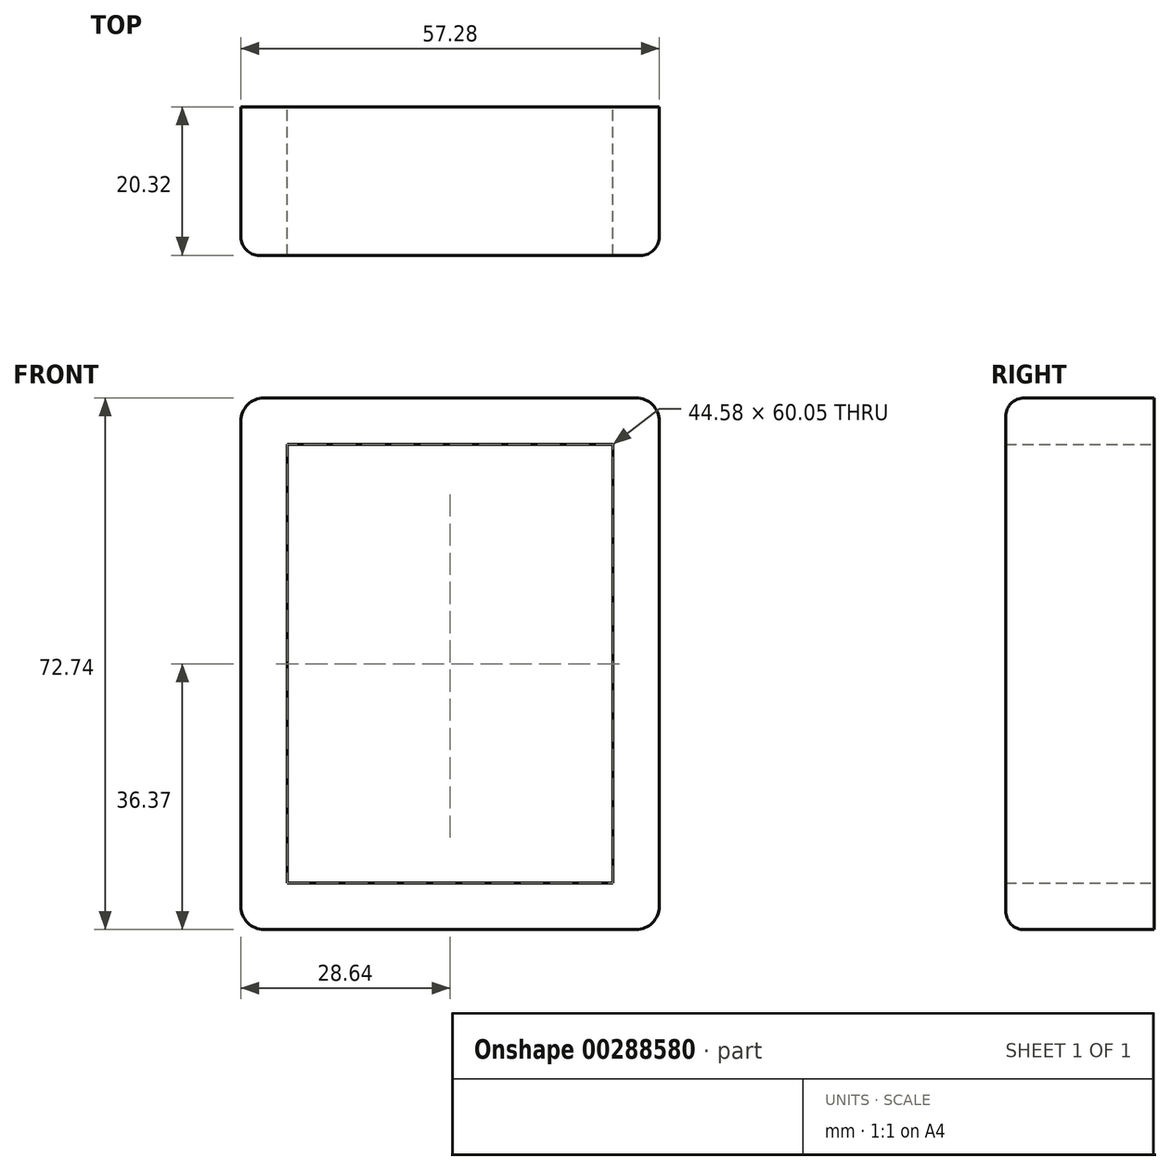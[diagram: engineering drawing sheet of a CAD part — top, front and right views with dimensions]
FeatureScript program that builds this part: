
annotation { "Feature Type Name" : "Feature", "Feature Type Description" : "" }
export const myFeature = defineFeature(function(context is Context, id is Id, definition is map)
    precondition{}
    {
        {
            var Q0;
            Q0=qCreatedBy(makeId("Front.planeOp"),FACE);
            var sketch = newSketch(context, id + "F0", { "sketchPlane" : qUnion([Q0])});
            skLineSegment(sketch, "E0.bottom", {"start": v(22.29, -30.02) * mm, "end": v(-22.29, -30.02) * mm});
            skLineSegment(sketch, "E0.top", {"start": v(22.29, 30.02) * mm, "end": v(-22.29, 30.02) * mm});
            skLineSegment(sketch, "E0.left", {"start": v(22.29, -30.02) * mm, "end": v(22.29, 30.02) * mm});
            skLineSegment(sketch, "E0.right", {"start": v(-22.29, -30.02) * mm, "end": v(-22.29, 30.02) * mm});
            skPoint(sketch, "E0.middle", {"position": v(0, 0) * mm});
            skLineSegment(sketch, "E1.0", {"start": v(28.64, -36.37) * mm, "end": v(28.64, 36.37) * mm});
            skLineSegment(sketch, "E1.1", {"start": v(28.64, -36.37) * mm, "end": v(-28.64, -36.37) * mm});
            skLineSegment(sketch, "E1.2", {"start": v(-28.64, -36.37) * mm, "end": v(-28.64, 36.37) * mm});
            skLineSegment(sketch, "E1.3", {"start": v(28.64, 36.37) * mm, "end": v(-28.64, 36.37) * mm});
            skSolve(sketch);
        }
        {
            var Q0;
            Q0=makeQuery(id+"F0.imprint","IMPRINT",FACE,{"disambiguationData":[TD([[makeQuery(id+"F0.imprint","IMPRINT",EDGE,{"derivedFrom":sQuery(id+"F0.wireOp",EDGE,"E0.bottom")}),1.0]])]});
            extrude(context, id + "F1", {"entities" : qUnion([Q0]), "depth" : 20.32 * mm});
        }
        {
            var Q0;
            Q0=makeQuery(id+"F1.opExtrude","SWEPT_EDGE",EDGE,{"disambiguationData":[OSD([sQuery(id+"F0.wireOp",EDGE,"E1.0"),sQuery(id+"F0.wireOp",EDGE,"E1.3")])]});
            var Q1;
            Q1=makeQuery(id+"F1.opExtrude","SWEPT_EDGE",EDGE,{"disambiguationData":[OSD([sQuery(id+"F0.wireOp",EDGE,"E1.0"),sQuery(id+"F0.wireOp",EDGE,"E1.1")])]});
            var Q2;
            Q2=makeQuery(id+"F1.opExtrude","SWEPT_EDGE",EDGE,{"disambiguationData":[OSD([sQuery(id+"F0.wireOp",EDGE,"E1.1"),sQuery(id+"F0.wireOp",EDGE,"E1.2")])]});
            var Q3;
            Q3=makeQuery(id+"F1.opExtrude","SWEPT_EDGE",EDGE,{"disambiguationData":[OSD([sQuery(id+"F0.wireOp",EDGE,"E1.2"),sQuery(id+"F0.wireOp",EDGE,"E1.3")])]});
            fillet(context, id + "F2", {"entities" : qUnion([Q0, Q1, Q2, Q3]), "radius" : 3.17 * mm, "tangentPropagation" : true, "allowEdgeOverflow" : false});
        }
        {
            var Q0;
            Q0=makeQuery(id+"F1.opExtrude","CAP_EDGE",EDGE,{"disambiguationData":[OSD([sQuery(id+"F0.wireOp",EDGE,"E1.3")])],"isStart":false});
            fillet(context, id + "F3", {"entities" : qUnion([Q0]), "radius" : 2.54 * mm, "tangentPropagation" : true, "allowEdgeOverflow" : false});
        }
    });
